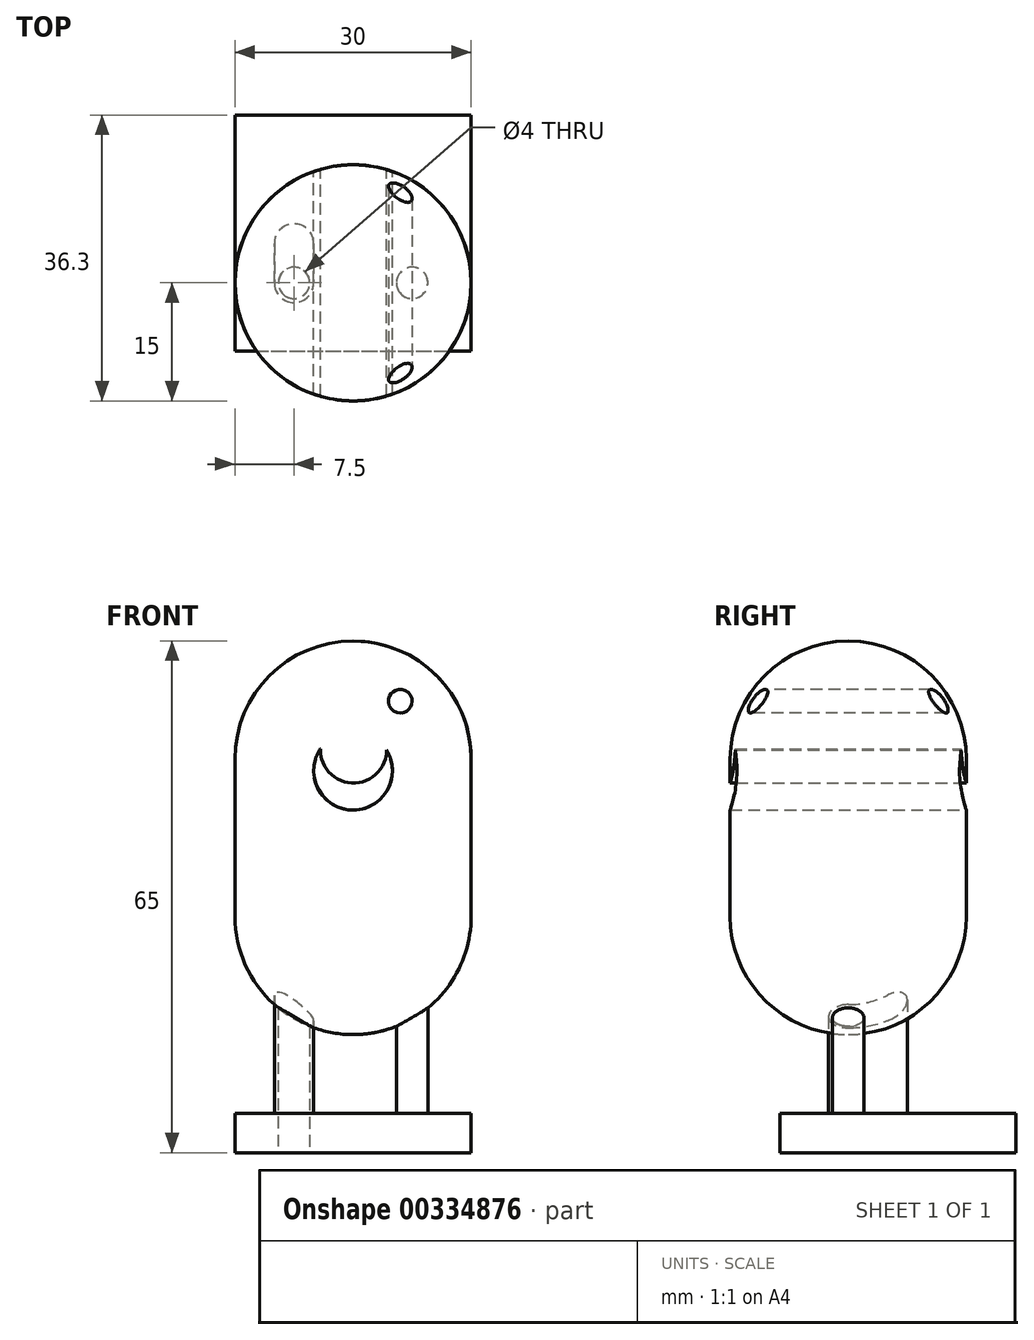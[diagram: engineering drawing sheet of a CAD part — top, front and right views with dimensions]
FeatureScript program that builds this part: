
annotation { "Feature Type Name" : "Feature", "Feature Type Description" : "" }
export const myFeature = defineFeature(function(context is Context, id is Id, definition is map)
    precondition{}
    {
        {
            var Q0;
            Q0=qCreatedBy(makeId("Top.planeOp"),FACE);
            var sketch = newSketch(context, id + "F0", { "sketchPlane" : qUnion([Q0])});
            skLineSegment(sketch, "E0", {"start": v(-15, 21.3) * mm, "end": v(-15, -8.7) * mm});
            skLineSegment(sketch, "E1", {"start": v(-15, -8.7) * mm, "end": v(15, -8.7) * mm});
            skLineSegment(sketch, "E2", {"start": v(15, -8.7) * mm, "end": v(15, 21.3) * mm});
            skLineSegment(sketch, "E3", {"start": v(15, 21.3) * mm, "end": v(-15, 21.3) * mm});
            skLineSegment(sketch, "E4.bottom", {"start": v(7.5, 7.5) * mm, "end": v(7.5, 7.5) * mm});
            skLineSegment(sketch, "E4.top", {"start": v(7.5, -2.5) * mm, "end": v(7.5, -2.5) * mm});
            skLineSegment(sketch, "E4.left", {"start": v(5, 5) * mm, "end": v(5, 0) * mm});
            skLineSegment(sketch, "E4.right", {"start": v(10, 5) * mm, "end": v(10, 0) * mm});
            skPoint(sketch, "E5.visualSharp", {"position": v(10, 7.5) * mm});
            skArc(sketch, "E5.filletArc", {"start": v(10, 5) * mm, "mid": v(9.27, 6.77) * mm, "end": v(7.5, 7.5) * mm});
            skPoint(sketch, "E6.visualSharp", {"position": v(5, 7.5) * mm});
            skArc(sketch, "E6.filletArc", {"start": v(7.5, 7.5) * mm, "mid": v(5.73, 6.77) * mm, "end": v(5, 5) * mm});
            skPoint(sketch, "E7.visualSharp", {"position": v(5, -2.5) * mm});
            skArc(sketch, "E7.filletArc", {"start": v(5, 0) * mm, "mid": v(5.73, -1.77) * mm, "end": v(7.5, -2.5) * mm});
            skPoint(sketch, "E8.visualSharp", {"position": v(10, -2.5) * mm});
            skArc(sketch, "E8.filletArc", {"start": v(7.5, -2.5) * mm, "mid": v(9.27, -1.77) * mm, "end": v(10, 0) * mm});
            skCircle(sketch, "E9", {"center": v(7.5, 0) * mm, "radius": 2 * mm});
            skArc(sketch, "E10.MirrorCS", {"start": v(-7.5, 7.5) * mm, "mid": v(-5.73, 6.77) * mm, "end": v(-5, 5) * mm});
            skArc(sketch, "E11.MirrorCS", {"start": v(-7.5, -2.5) * mm, "mid": v(-9.27, -1.77) * mm, "end": v(-10, 0) * mm});
            skArc(sketch, "E12.MirrorCS", {"start": v(-5, 0) * mm, "mid": v(-5.73, -1.77) * mm, "end": v(-7.5, -2.5) * mm});
            skCircle(sketch, "E13.MirrorC", {"center": v(-7.5, 0) * mm, "radius": 2 * mm});
            skLineSegment(sketch, "E14.MirrorCS", {"start": v(-10, 5) * mm, "end": v(-10, 0) * mm});
            skLineSegment(sketch, "E15.MirrorCS", {"start": v(-5, 5) * mm, "end": v(-5, 0) * mm});
            skPoint(sketch, "E16.MirrorP", {"position": v(-5, 7.5) * mm});
            skArc(sketch, "E17.MirrorCS", {"start": v(-10, 5) * mm, "mid": v(-9.27, 6.77) * mm, "end": v(-7.5, 7.5) * mm});
            skPoint(sketch, "E18.MirrorP", {"position": v(-10, 7.5) * mm});
            skPoint(sketch, "E19.MirrorP", {"position": v(-5, -2.5) * mm});
            skPoint(sketch, "E20.MirrorP", {"position": v(-10, -2.5) * mm});
            skSolve(sketch);
        }
        {
            var Q0;
            Q0=makeQuery(id+"F0.imprint","IMPRINT",FACE,{"disambiguationData":[TD([[makeQuery(id+"F0.imprint","IMPRINT",EDGE,{"derivedFrom":sQuery(id+"F0.wireOp",EDGE,"E0")}),1.0]])]});
            var Q1;
            {var subQ0=sQuery(id+"F0.wireOp",EDGE,"UguDD5Zi-KEHb-qlkr-ukyR-XNeW6nje3KCY");Q1=makeQuery(id+"F0.imprint","IMPRINT",FACE,{"disambiguationData":[TD([[makeQuery(id+"F0.imprint","IMPRINT",EDGE,{"derivedFrom":subQ0}),1.0]])]});}
            var Q2;
            {var subQ0=sQuery(id+"F0.wireOp",EDGE,"Yqz7lN83-afWR-3hmQ-tsRn-bF2yiUwXfHW3");Q2=makeQuery(id+"F0.imprint","IMPRINT",FACE,{"disambiguationData":[TD([[makeQuery(id+"F0.imprint","IMPRINT",EDGE,{"derivedFrom":subQ0}),1.0]])]});}
            var Q3;
            {var subQ0=sQuery(id+"F0.wireOp",EDGE,"ecd2eff0-9319-44bc-b762-77e20afb071d");Q3=makeQuery(id+"F0.imprint","IMPRINT",FACE,{"disambiguationData":[TD([[makeQuery(id+"F0.imprint","IMPRINT",EDGE,{"derivedFrom":subQ0}),1.0]])]});}
            var Q4;
            {var subQ0=sQuery(id+"F0.wireOp",EDGE,"6c9bac5a-8e61-405f-a2a0-1be64b94ba85");Q4=makeQuery(id+"F0.imprint","IMPRINT",FACE,{"disambiguationData":[TD([[makeQuery(id+"F0.imprint","IMPRINT",EDGE,{"derivedFrom":subQ0}),1.0]])]});}
            var Q5;
            {var subQ0=sQuery(id+"F0.wireOp",EDGE,"0bcb4b9b-7856-4a44-a33c-78db76905be1");var subQ1=makeQuery(id+"F0.imprint","INTERSECT",VERTEX,{"derivedFrom":[sQuery(id+"F0.wireOp",EDGE,"7hP1voKO-S6D5-9DZY-zVUw-l0Q5b9ZxMXaU"),subQ0]});Q5=makeQuery(id+"F0.imprint","IMPRINT",FACE,{"disambiguationData":[TD([[makeQuery(id+"F0.imprint","IMPRINT",EDGE,{"disambiguationData":[TD([[subQ1,1.0]])],"derivedFrom":subQ0}),1.0]])]});}
            var Q6;
            {var subQ0=sQuery(id+"F0.wireOp",EDGE,"f4b36cdf-c5c3-4683-b204-f700a1aba58c");var subQ1=makeQuery(id+"F0.imprint","INTERSECT",VERTEX,{"derivedFrom":[sQuery(id+"F0.wireOp",EDGE,"c943a1da-361b-4ca5-9757-ff5da4a47179"),subQ0]});Q6=makeQuery(id+"F0.imprint","IMPRINT",FACE,{"disambiguationData":[TD([[makeQuery(id+"F0.imprint","IMPRINT",EDGE,{"disambiguationData":[TD([[subQ1,1.0]])],"derivedFrom":subQ0}),1.0]])]});}
            extrude(context, id + "F1", {"entities" : qUnion([Q0, Q1, Q2, Q3, Q4, Q5, Q6]), "depth" : 2 * mm});
        }
        {
            var Q0;
            Q0=qCreatedBy(makeId("Front.planeOp"),FACE);
            var sketch = newSketch(context, id + "F2", { "sketchPlane" : qUnion([Q0])});
            skLineSegment(sketch, "E21.bottom", {"start": v(0, 65) * mm, "end": v(0, 65) * mm});
            skLineSegment(sketch, "E21.top", {"start": v(0, 15) * mm, "end": v(0, 15) * mm});
            skLineSegment(sketch, "E21.left", {"start": v(0, 65) * mm, "end": v(0, 15) * mm});
            skLineSegment(sketch, "E21.right", {"start": v(15, 50) * mm, "end": v(15, 30) * mm});
            skPoint(sketch, "E22.visualSharp", {"position": v(15, 65) * mm});
            skArc(sketch, "E22.filletArc", {"start": v(15, 50) * mm, "mid": v(10.6, 60.6) * mm, "end": v(0, 65) * mm});
            skPoint(sketch, "E23.visualSharp", {"position": v(15, 15) * mm});
            skArc(sketch, "E23.filletArc", {"start": v(0, 15) * mm, "mid": v(10.6, 19.4) * mm, "end": v(15, 30) * mm});
            skCircle(sketch, "E24", {"center": v(6, 57.35) * mm, "radius": 1.5 * mm});
            skCircle(sketch, "E25.MirrorC", {"center": v(-6, 57.35) * mm, "radius": 1.5 * mm});
            skArc(sketch, "E26", {"start": v(4.27, 51.13) * mm, "mid": v(-0.1, 43.53) * mm, "end": v(-4.15, 51.3) * mm});
            skArc(sketch, "E27", {"start": v(-4.15, 51.3) * mm, "mid": v(-0.03, 46.95) * mm, "end": v(4.27, 51.13) * mm});
            skSolve(sketch);
        }
        {
            var Q0;
            Q0=makeQuery(id+"F0.imprint","IMPRINT",FACE,{"disambiguationData":[TD([[makeQuery(id+"F0.imprint","IMPRINT",EDGE,{"derivedFrom":sQuery(id+"F0.wireOp",EDGE,"E4.left")}),1.0]])]});
            var Q1;
            Q1=makeQuery(id+"F0.imprint","IMPRINT",FACE,{"disambiguationData":[TD([[makeQuery(id+"F0.imprint","IMPRINT",EDGE,{"derivedFrom":sQuery(id+"F0.wireOp",EDGE,"E10.MirrorCS")}),-1.0]])]});
            extrude(context, id + "F3", {"entities" : qUnion([Q0, Q1]), "operationType" : NewBodyOperationType.ADD, "depth" : 5 * mm});
        }
        {
            var Q0;
            Q0=makeQuery(id+"F0.imprint","IMPRINT",FACE,{"disambiguationData":[TD([[makeQuery(id+"F0.imprint","IMPRINT",EDGE,{"derivedFrom":sQuery(id+"F0.wireOp",EDGE,"E9")}),1.0]])]});
            var Q1;
            Q1=makeQuery(id+"F0.imprint","IMPRINT",FACE,{"disambiguationData":[TD([[makeQuery(id+"F0.imprint","IMPRINT",EDGE,{"derivedFrom":sQuery(id+"F0.wireOp",EDGE,"E13.MirrorC")}),-1.0]])]});
            extrude(context, id + "F4", {"entities" : qUnion([Q0, Q1]), "operationType" : NewBodyOperationType.ADD, "depth" : 25 * mm});
        }
        {
            var Q0;
            Q0=makeQuery(id+"F2.imprint","IMPRINT",FACE,{"disambiguationData":[TD([[makeQuery(id+"F2.imprint","IMPRINT",EDGE,{"derivedFrom":sQuery(id+"F2.wireOp",EDGE,"E21.left")}),1.0]])]});
            var Q1;
            Q1=makeQuery(id+"F2.imprint","IMPRINT",FACE,{"disambiguationData":[TD([[makeQuery(id+"F2.imprint","IMPRINT",EDGE,{"derivedFrom":sQuery(id+"F2.wireOp",EDGE,"E24")}),1.0]])]});
            var Q2;
            {var subQ0=sQuery(id+"F2.wireOp",EDGE,"E27");var subQ1=sQuery(id+"F2.wireOp",EDGE,"E21.left");var subQ2=makeQuery(id+"F2.imprint","INTERSECT",VERTEX,{"derivedFrom":[subQ1,subQ0]});Q2=makeQuery(id+"F2.imprint","IMPRINT",FACE,{"disambiguationData":[TD([[makeQuery(id+"F2.imprint","IMPRINT",EDGE,{"disambiguationData":[TD([[subQ2,-1.0]])],"derivedFrom":subQ1}),1.0]])]});}
            var Q3;
            Q3=sQuery(id+"F2.wireOp",EDGE,"E21.left");
            revolve(context, id + "F5", {"operationType" : NewBodyOperationType.ADD, "entities" : qUnion([Q0, Q1, Q2]), "axis" : qUnion([Q3]), "revolveType" : RevolveType.FULL});
        }
        {
            var Q0;
            Q0=makeQuery(id+"F2.imprint","IMPRINT",FACE,{"disambiguationData":[TD([[makeQuery(id+"F2.imprint","IMPRINT",EDGE,{"derivedFrom":sQuery(id+"F2.wireOp",EDGE,"E24")}),1.0]])]});
            var Q1;
            Q1=makeQuery(id+"F2.imprint","IMPRINT",FACE,{"disambiguationData":[TD([[makeQuery(id+"F2.imprint","IMPRINT",EDGE,{"derivedFrom":sQuery(id+"F2.wireOp",EDGE,"E25.MirrorC")}),-1.0]])]});
            extrude(context, id + "F6", {"entities" : qUnion([Q0, Q1]), "operationType" : NewBodyOperationType.REMOVE, "endBound" : BoundingType.SYMMETRIC, "oppositeDirection" : true, "depth" : 30 * mm});
        }
        {
            var Q0;
            {var subQ0=sQuery(id+"F2.wireOp",EDGE,"E27");var subQ1=sQuery(id+"F2.wireOp",EDGE,"E21.left");var subQ2=makeQuery(id+"F2.imprint","INTERSECT",VERTEX,{"derivedFrom":[subQ1,subQ0]});Q0=makeQuery(id+"F2.imprint","IMPRINT",FACE,{"disambiguationData":[TD([[makeQuery(id+"F2.imprint","IMPRINT",EDGE,{"disambiguationData":[TD([[subQ2,-1.0]])],"derivedFrom":subQ1}),1.0]])]});}
            var Q1;
            {var subQ0=sQuery(id+"F2.wireOp",EDGE,"E27");var subQ1=sQuery(id+"F2.wireOp",EDGE,"E21.left");var subQ2=makeQuery(id+"F2.imprint","INTERSECT",VERTEX,{"derivedFrom":[subQ1,subQ0]});Q1=makeQuery(id+"F2.imprint","IMPRINT",FACE,{"disambiguationData":[TD([[makeQuery(id+"F2.imprint","IMPRINT",EDGE,{"disambiguationData":[TD([[subQ2,-1.0]])],"derivedFrom":subQ1}),-1.0]])]});}
            extrude(context, id + "F7", {"entities" : qUnion([Q0, Q1]), "operationType" : NewBodyOperationType.REMOVE, "endBound" : BoundingType.SYMMETRIC, "depth" : 30 * mm});
        }
    });
